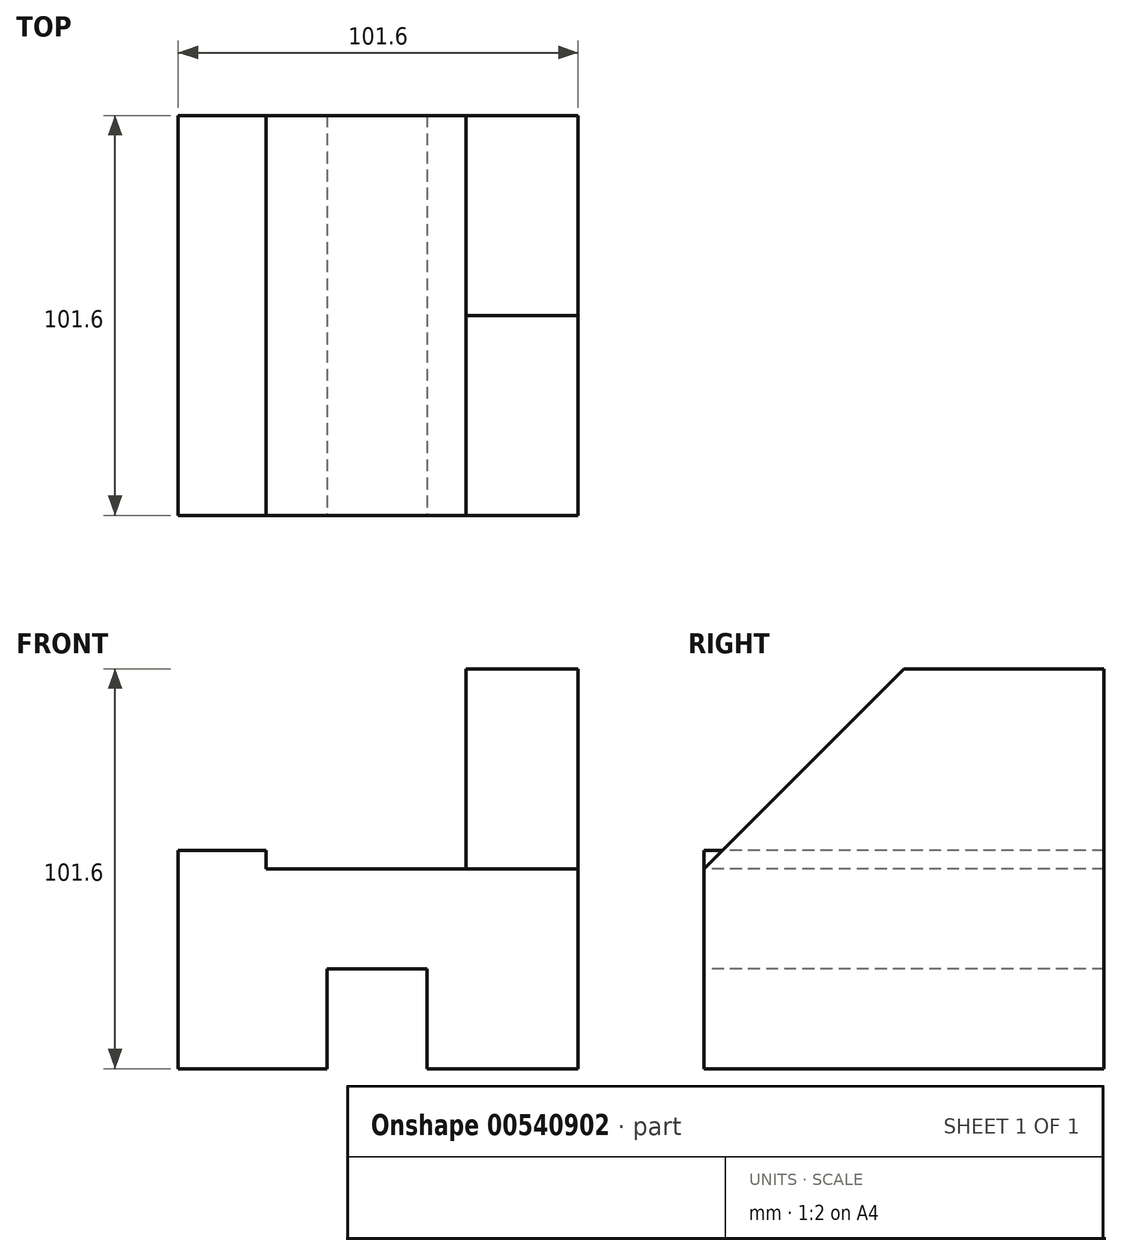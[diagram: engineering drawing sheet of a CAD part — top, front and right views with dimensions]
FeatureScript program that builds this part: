
annotation { "Feature Type Name" : "Feature", "Feature Type Description" : "" }
export const myFeature = defineFeature(function(context is Context, id is Id, definition is map)
    precondition{}
    {
        {
            var Q0;
            Q0=qCreatedBy(makeId("Top.planeOp"),FACE);
            var sketch = newSketch(context, id + "F0", { "sketchPlane" : qUnion([Q0])});
            skLineSegment(sketch, "E0.bottom", {"start": v(0, 0) * mm, "end": v(-101.6, 0) * mm});
            skLineSegment(sketch, "E0.top", {"start": v(0, -101.6) * mm, "end": v(-101.6, -101.6) * mm});
            skLineSegment(sketch, "E0.left", {"start": v(0, 0) * mm, "end": v(0, -101.6) * mm});
            skLineSegment(sketch, "E0.right", {"start": v(-101.6, 0) * mm, "end": v(-101.6, -101.6) * mm});
            skSolve(sketch);
        }
        {
            var Q0;
            Q0 = qSketchRegion(id + "F0", true);
            extrude(context, id + "F1", {"entities" : qUnion([Q0]), "depth" : 101.6 * mm, "offsetDistance" : 25.4 * mm});
        }
        {
            var Q0;
            Q0=makeQuery(id+"F1.opExtrude","SWEPT_FACE",FACE,{"disambiguationData":[OSD([sQuery(id+"F0.wireOp",EDGE,"E0.top")])]});
            var sketch = newSketch(context, id + "F2", { "sketchPlane" : qUnion([Q0])});
            skLineSegment(sketch, "E1.bottom", {"start": v(-63.78, 0) * mm, "end": v(-38.38, 0) * mm});
            skLineSegment(sketch, "E1.top", {"start": v(-63.78, 25.4) * mm, "end": v(-38.38, 25.4) * mm});
            skLineSegment(sketch, "E1.left", {"start": v(-63.78, 0) * mm, "end": v(-63.78, 25.4) * mm});
            skLineSegment(sketch, "E1.right", {"start": v(-38.38, 0) * mm, "end": v(-38.38, 25.4) * mm});
            skSolve(sketch);
        }
        {
            var Q0;
            Q0=makeQuery(id+"F2.imprint","IMPRINT",FACE,{"disambiguationData":[TD([[makeQuery(id+"F2.imprint","IMPRINT",EDGE,{"derivedFrom":sQuery(id+"F2.wireOp",EDGE,"E1.bottom")}),-1.0]])]});
            extrude(context, id + "F3", {"entities" : qUnion([Q0]), "operationType" : NewBodyOperationType.REMOVE, "oppositeDirection" : true, "depth" : 232.92 * mm, "offsetDistance" : 25.4 * mm});
        }
        {
            var Q0;
            Q0=makeQuery(id+"F1.opExtrude","SWEPT_FACE",FACE,{"disambiguationData":[OSD([sQuery(id+"F0.wireOp",EDGE,"E0.top")])]});
            var sketch = newSketch(context, id + "F4", { "sketchPlane" : qUnion([Q0])});
            skLineSegment(sketch, "E2.bottom", {"start": v(-101.6, 101.6) * mm, "end": v(-79.27, 101.6) * mm});
            skLineSegment(sketch, "E2.top", {"start": v(-101.6, 55.4) * mm, "end": v(-79.27, 55.4) * mm});
            skLineSegment(sketch, "E2.left", {"start": v(-101.6, 101.6) * mm, "end": v(-101.6, 55.4) * mm});
            skLineSegment(sketch, "E2.right", {"start": v(-79.27, 101.6) * mm, "end": v(-79.27, 55.4) * mm});
            skSolve(sketch);
        }
        {
            var Q0;
            Q0=makeQuery(id+"F4.imprint","IMPRINT",FACE,{"disambiguationData":[TD([[makeQuery(id+"F4.imprint","IMPRINT",EDGE,{"derivedFrom":sQuery(id+"F4.wireOp",EDGE,"E2.bottom")}),1.0]])]});
            extrude(context, id + "F5", {"entities" : qUnion([Q0]), "operationType" : NewBodyOperationType.REMOVE, "oppositeDirection" : true, "depth" : 115.82 * mm, "offsetDistance" : 25.4 * mm});
        }
        {
            var Q0;
            Q0=makeQuery(id+"F1.opExtrude","SWEPT_FACE",FACE,{"disambiguationData":[OSD([sQuery(id+"F0.wireOp",EDGE,"E0.top")])]});
            var sketch = newSketch(context, id + "F6", { "sketchPlane" : qUnion([Q0])});
            skLineSegment(sketch, "E3.bottom", {"start": v(-79.27, 101.6) * mm, "end": v(-28.47, 101.6) * mm});
            skLineSegment(sketch, "E3.top", {"start": v(-79.27, 50.8) * mm, "end": v(-28.47, 50.8) * mm});
            skLineSegment(sketch, "E3.left", {"start": v(-79.27, 101.6) * mm, "end": v(-79.27, 50.8) * mm});
            skLineSegment(sketch, "E3.right", {"start": v(-28.47, 101.6) * mm, "end": v(-28.47, 50.8) * mm});
            skSolve(sketch);
        }
        {
            var Q0;
            {var subQ3=sQuery(id+"F6.wireOp",EDGE,"E3.bottom");Q0=makeQuery(id+"F6.imprint","IMPRINT",FACE,{"disambiguationData":[TD([[makeQuery(id+"F6.imprint","IMPRINT",EDGE,{"derivedFrom":subQ3}),1.0]])]});}
            extrude(context, id + "F7", {"entities" : qUnion([Q0]), "operationType" : NewBodyOperationType.REMOVE, "oppositeDirection" : true, "depth" : 154.94 * mm, "offsetDistance" : 25.4 * mm});
        }
        {
            var Q0;
            Q0=makeQuery(id+"F1.opExtrude","SWEPT_FACE",FACE,{"disambiguationData":[OSD([sQuery(id+"F0.wireOp",EDGE,"E0.left")])]});
            var sketch = newSketch(context, id + "F8", { "sketchPlane" : qUnion([Q0])});
            skLineSegment(sketch, "E4", {"start": v(-101.6, 0) * mm, "end": v(-101.6, 50.8) * mm});
            skLineSegment(sketch, "E5", {"start": v(-101.6, 50.8) * mm, "end": v(-50.8, 101.6) * mm});
            skSolve(sketch);
        }
        {
            var Q0;
            {var subQ0=sQuery(id+"F8.wireOp",EDGE,"E5");Q0=makeQuery(id+"F8.imprint","IMPRINT",FACE,{"disambiguationData":[TD([[makeQuery(id+"F8.imprint","IMPRINT",EDGE,{"derivedFrom":subQ0}),1.0]])]});}
            extrude(context, id + "F9", {"entities" : qUnion([Q0]), "operationType" : NewBodyOperationType.REMOVE, "oppositeDirection" : true, "depth" : 54.36 * mm, "offsetDistance" : 25.4 * mm});
        }
    });
